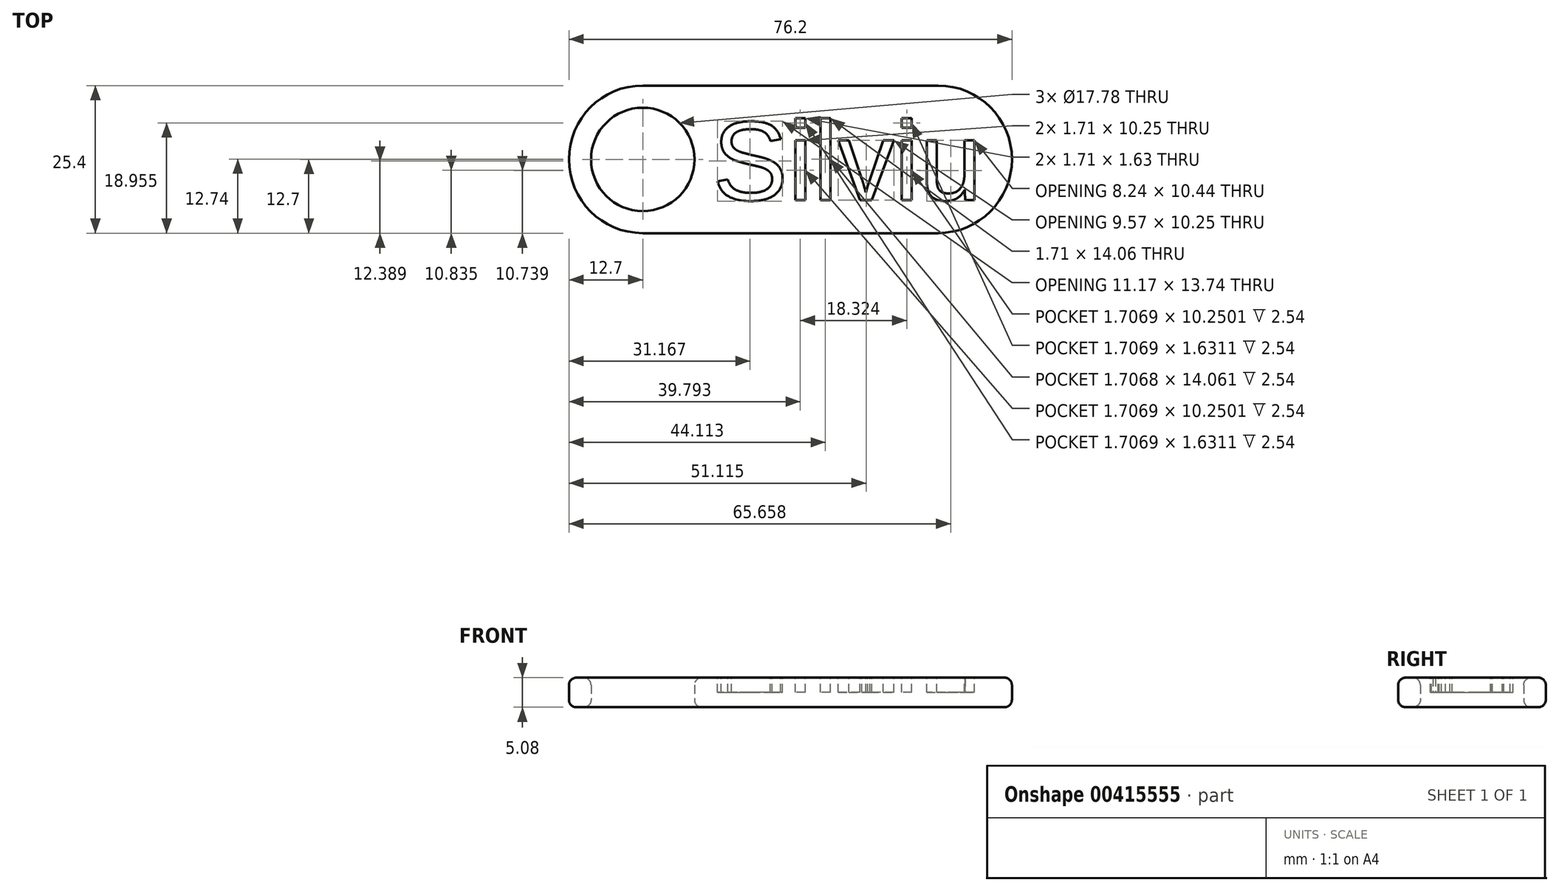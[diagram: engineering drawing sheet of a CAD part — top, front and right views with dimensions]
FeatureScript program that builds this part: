
annotation { "Feature Type Name" : "Feature", "Feature Type Description" : "" }
export const myFeature = defineFeature(function(context is Context, id is Id, definition is map)
    precondition{}
    {
        {
            var Q0;
            Q0=qCreatedBy(makeId("Top.planeOp"),FACE);
            var sketch = newSketch(context, id + "F0", { "sketchPlane" : qUnion([Q0])});
            skLineSegment(sketch, "E0.bottom", {"start": v(25.4, -12.7) * mm, "end": v(-25.4, -12.7) * mm});
            skLineSegment(sketch, "E0.top", {"start": v(25.4, 12.7) * mm, "end": v(-25.4, 12.7) * mm});
            skPoint(sketch, "E0.middle", {"position": v(0, 0) * mm});
            skArc(sketch, "E1", {"start": v(25.4, -12.7) * mm, "mid": v(38.1, 0) * mm, "end": v(25.4, 12.7) * mm});
            skArc(sketch, "E2", {"start": v(-25.4, 12.7) * mm, "mid": v(-38.1, 0) * mm, "end": v(-25.4, -12.7) * mm});
            skCircle(sketch, "E3", {"center": v(-25.4, 0) * mm, "radius": 8.9 * mm});
            skSolve(sketch);
        }
        {
            var Q0;
            Q0=makeQuery(id+"F0.imprint","IMPRINT",FACE,{"disambiguationData":[TD([[makeQuery(id+"F0.imprint","IMPRINT",EDGE,{"derivedFrom":sQuery(id+"F0.wireOp",EDGE,"E0.bottom")}),-1.0]])]});
            extrude(context, id + "F1", {"entities" : qUnion([Q0]), "depth" : 5.08 * mm});
        }
        {
            var Q0;
            Q0=makeQuery(id+"F1.opExtrude","CAP_FACE",FACE,{"disambiguationData":[OSD([sQuery(id+"F0.wireOp",EDGE,"E0.bottom"),sQuery(id+"F0.wireOp",EDGE,"E0.top"),sQuery(id+"F0.wireOp",EDGE,"E1"),sQuery(id+"F0.wireOp",EDGE,"E2"),sQuery(id+"F0.wireOp",EDGE,"E3")])],"isStart":false});
            var sketch = newSketch(context, id + "F2", { "sketchPlane" : qUnion([Q0])});
            skText(sketch, "E4", { "text": "Silviu", "fontName": "Arimo-Regular.ttf"});
            const initialGuessF2  = {"E4": [-0.0134, -0.00699, 1, 0, 0.01397]};
            skSetInitialGuess(sketch, initialGuessF2);
            skSolve(sketch);
        }
        {
            var Q0;
            Q0=qSketchRegion(id+"F2",true);
            extrude(context, id + "F3", {"entities" : qUnion([Q0]), "operationType" : NewBodyOperationType.REMOVE, "oppositeDirection" : true, "depth" : 2.54 * mm});
        }
        {
            var Q0;
            Q0=makeQuery(id+"F1.opExtrude","CAP_EDGE",EDGE,{"disambiguationData":[OSD([sQuery(id+"F0.wireOp",EDGE,"E2")])],"isStart":false});
            var Q1;
            Q1=makeQuery(id+"F1.opExtrude","CAP_FACE",FACE,{"disambiguationData":[OSD([sQuery(id+"F0.wireOp",EDGE,"E0.bottom"),sQuery(id+"F0.wireOp",EDGE,"E0.top"),sQuery(id+"F0.wireOp",EDGE,"E1"),sQuery(id+"F0.wireOp",EDGE,"E2"),sQuery(id+"F0.wireOp",EDGE,"E3")])],"isStart":true});
            var Q2;
            Q2=makeQuery(id+"F1.opExtrude","CAP_EDGE",EDGE,{"disambiguationData":[OSD([sQuery(id+"F0.wireOp",EDGE,"E3")])],"isStart":false});
            fillet(context, id + "F4", {"entities" : qUnion([Q0, Q1, Q2]), "radius" : 1.27 * mm, "tangentPropagation" : true, "allowEdgeOverflow" : false});
        }
    });
